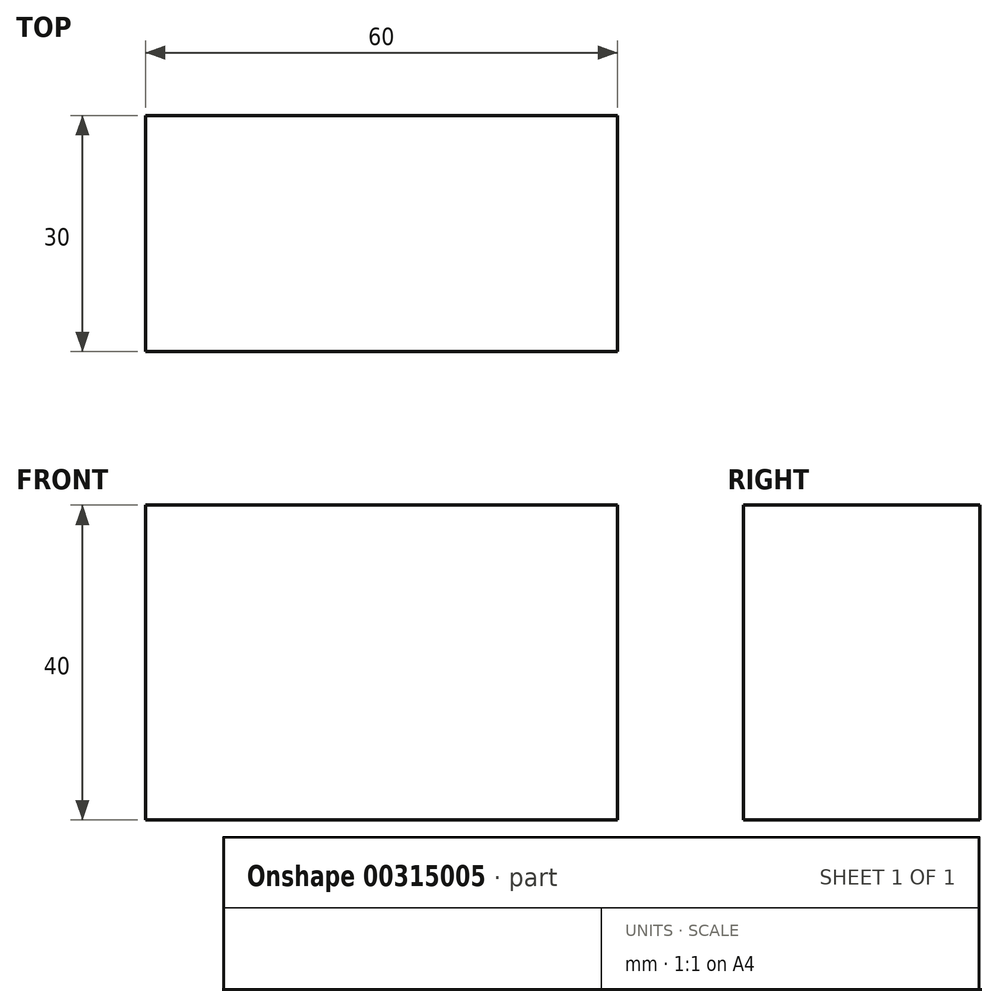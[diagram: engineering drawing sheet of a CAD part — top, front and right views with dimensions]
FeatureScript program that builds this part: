
annotation { "Feature Type Name" : "Feature", "Feature Type Description" : "" }
export const myFeature = defineFeature(function(context is Context, id is Id, definition is map)
    precondition{}
    {
        {
            var Q0;
            Q0=qCreatedBy(makeId("Front.planeOp"),FACE);
            var sketch = newSketch(context, id + "F0", { "sketchPlane" : qUnion([Q0])});
            skLineSegment(sketch, "E0.bottom", {"start": v(0.3, 0.03) * mm, "end": v(60.3, 0.03) * mm});
            skLineSegment(sketch, "E0.top", {"start": v(0.3, -39.97) * mm, "end": v(60.3, -39.97) * mm});
            skLineSegment(sketch, "E0.left", {"start": v(0.3, 0.03) * mm, "end": v(0.3, -39.97) * mm});
            skLineSegment(sketch, "E0.right", {"start": v(60.3, 0.03) * mm, "end": v(60.3, -39.97) * mm});
            skSolve(sketch);
        }
        {
            var Q0;
            Q0=makeQuery(id+"F0.imprint","IMPRINT",FACE,{"disambiguationData":[TD([[makeQuery(id+"F0.imprint","IMPRINT",EDGE,{"derivedFrom":sQuery(id+"F0.wireOp",EDGE,"E0.bottom")}),-1.0]])]});
            extrude(context, id + "F1", {"entities" : qUnion([Q0]), "depth" : 30 * mm});
        }
    });
